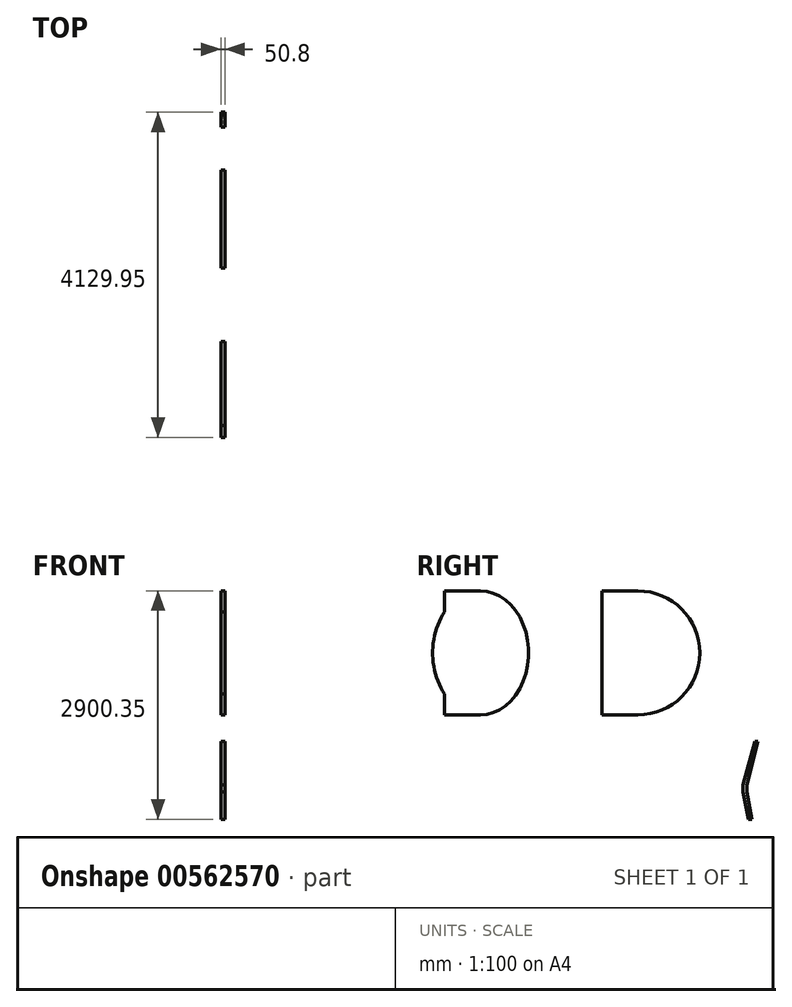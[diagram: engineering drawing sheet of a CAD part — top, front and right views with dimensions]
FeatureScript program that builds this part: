
annotation { "Feature Type Name" : "Feature", "Feature Type Description" : "" }
export const myFeature = defineFeature(function(context is Context, id is Id, definition is map)
    precondition{}
    {
        {
            var Q0;
            Q0=qCreatedBy(makeId("Right.planeOp"),FACE);
            var sketch = newSketch(context, id + "F0", { "sketchPlane" : qUnion([Q0])});
            skLineSegment(sketch, "E0", {"start": v(0, 0) * mm, "end": v(0, 1574.8) * mm});
            skLineSegment(sketch, "E1", {"start": v(0, 1574.8) * mm, "end": v(457.2, 1574.8) * mm});
            skLineSegment(sketch, "E2", {"start": v(0, 0) * mm, "end": v(457.2, 0) * mm});
            skArc(sketch, "E3", {"start": v(457.2, 1574.8) * mm, "mid": v(1244.6, 787.4) * mm, "end": v(457.2, 0) * mm});
            skLineSegment(sketch, "E4", {"start": v(-1997.37, 0) * mm, "end": v(-1997.37, 1574.8) * mm});
            skLineSegment(sketch, "E5", {"start": v(-1997.37, 1574.8) * mm, "end": v(-1540.17, 1574.8) * mm});
            skLineSegment(sketch, "E6", {"start": v(-1997.37, 0) * mm, "end": v(-1540.17, 0) * mm});
            skLineSegment(sketch, "E7", {"start": v(-1997.37, 787.4) * mm, "end": v(-930.57, 787.4) * mm});
            skLineSegment(sketch, "E8", {"start": v(-1997.37, 787.4) * mm, "end": v(-1463.97, 787.4) * mm});
            skLineSegment(sketch, "E9", {"start": v(-1997.37, 787.4) * mm, "end": v(-1540.17, 787.4) * mm});
            skEllipse(sketch, "E10", {"center": v(-1540.17, 787.4) * mm, "majorRadius": 787.4 * mm, "minorRadius": 609.6 * mm, "majorAxis": v(0, -1)});
            skLineSegment(sketch, "E11", {"start": v(1840.48, -887.4) * mm, "end": v(1840.48, -976.3) * mm});
            skLineSegment(sketch, "E12", {"start": v(1840.48, -887.4) * mm, "end": v(1980.18, -334.95) * mm});
            skLineSegment(sketch, "E13", {"start": v(1840.48, -976.3) * mm, "end": v(1903.98, -1325.55) * mm});
            skLineSegment(sketch, "E14", {"start": v(1789.68, -976.3) * mm, "end": v(1789.68, -887.4) * mm});
            skLineSegment(sketch, "E15", {"start": v(1789.68, -887.4) * mm, "end": v(1942.08, -334.95) * mm});
            skLineSegment(sketch, "E16", {"start": v(1789.68, -976.3) * mm, "end": v(1859.53, -1325.55) * mm});
            skLineSegment(sketch, "E17", {"start": v(1859.53, -1325.55) * mm, "end": v(1903.98, -1325.55) * mm});
            skLineSegment(sketch, "E18", {"start": v(1942.08, -334.95) * mm, "end": v(1980.18, -334.95) * mm});
            skSolve(sketch);
        }
        {
            var Q0;
            Q0 = qSketchRegion(id + "F0", true);
            extrude(context, id + "F1", {"entities" : qUnion([Q0]), "depth" : 50.8 * mm, "offsetDistance" : 25.4 * mm});
        }
    });
